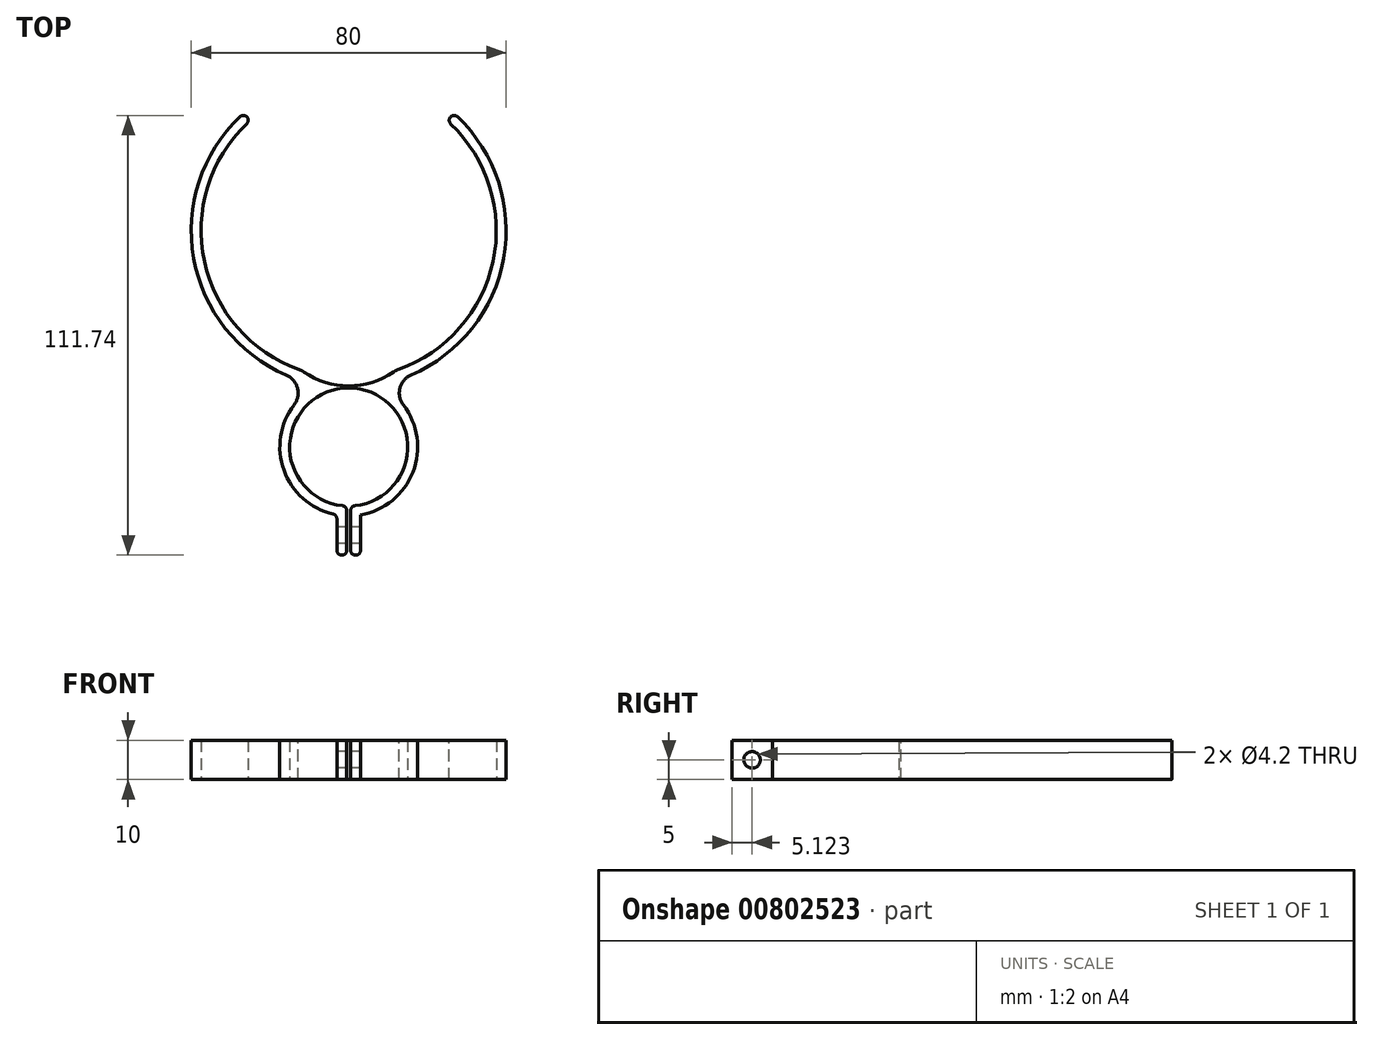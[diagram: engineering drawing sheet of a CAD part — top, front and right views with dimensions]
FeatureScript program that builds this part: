
annotation { "Feature Type Name" : "Feature", "Feature Type Description" : "" }
export const myFeature = defineFeature(function(context is Context, id is Id, definition is map)
    precondition{}
    {
        {
            var Q0;
            Q0=qCreatedBy(makeId("Top.planeOp"),FACE);
            var sketch = newSketch(context, id + "F0", { "sketchPlane" : qUnion([Q0])});
            skCircle(sketch, "E0", {"center": v(0, 0) * mm, "radius": 1.25 * mm});
            skArc(sketch, "E1", {"start": v(0, -1.25) * mm, "mid": v(-15, -16) * mm, "end": v(-0.5, -31.24) * mm});
            skArc(sketch, "E2.0", {"start": v(0, 1.25) * mm, "mid": v(-17.5, -16) * mm, "end": v(-0.5, -33.74) * mm});
            skArc(sketch, "E3", {"start": v(0, 76.25) * mm, "mid": v(-37.5, 38.75) * mm, "end": v(0, 1.25) * mm});
            skArc(sketch, "E4.0", {"start": v(0, 78.75) * mm, "mid": v(-40, 38.75) * mm, "end": v(0, -1.25) * mm});
            skLineSegment(sketch, "E5", {"start": v(0, 78.75) * mm, "end": v(0, 76.25) * mm});
            skLineSegment(sketch, "E6.bottom", {"start": v(-0.5, -31.24) * mm, "end": v(-3, -31.24) * mm});
            skLineSegment(sketch, "E6.top", {"start": v(-0.5, -43.74) * mm, "end": v(-3, -43.74) * mm});
            skLineSegment(sketch, "E6.left", {"start": v(-0.5, -31.24) * mm, "end": v(-0.5, -43.74) * mm});
            skLineSegment(sketch, "E6.right", {"start": v(-3, -31.24) * mm, "end": v(-3, -43.74) * mm});
            skPoint(sketch, "E7", {"position": v(-0.5, -33.74) * mm});
            skPoint(sketch, "E8.orphan", {"position": v(0, -31.25) * mm});
            skArc(sketch, "E9.MirrorCS", {"start": v(0, 76.25) * mm, "mid": v(37.5, 38.75) * mm, "end": v(0, 1.25) * mm});
            skArc(sketch, "E10.MirrorCS", {"start": v(0, 78.75) * mm, "mid": v(40, 38.75) * mm, "end": v(0, -1.25) * mm});
            skArc(sketch, "E11.MirrorCS", {"start": v(0, -1.25) * mm, "mid": v(15, -16) * mm, "end": v(0.5, -31.24) * mm});
            skArc(sketch, "E12.MirrorCS", {"start": v(0, 1.25) * mm, "mid": v(17.5, -16) * mm, "end": v(0.5, -33.74) * mm});
            skLineSegment(sketch, "E13.MirrorCS", {"start": v(3, -31.24) * mm, "end": v(3, -43.74) * mm});
            skLineSegment(sketch, "E14.MirrorCS", {"start": v(0.5, -31.24) * mm, "end": v(0.5, -43.74) * mm});
            skLineSegment(sketch, "E15.MirrorCS", {"start": v(0.5, -43.74) * mm, "end": v(3, -43.74) * mm});
            skSolve(sketch);
        }
        {
            var Q0;
            Q0=qSketchRegion(id+"F0",true);
            extrude(context, id + "F1", {"entities" : qUnion([Q0]), "depth" : 10 * mm, "offsetDistance" : 25 * mm});
        }
        {
            var Q0;
            Q0=qCreatedBy(makeId("Top.planeOp"),FACE);
            var sketch = newSketch(context, id + "F2", { "sketchPlane" : qUnion([Q0])});
            skLineSegment(sketch, "E16.bottom", {"start": v(-22.5, 68.75) * mm, "end": v(22.5, 68.75) * mm, "construction": true});
            skLineSegment(sketch, "E16.top", {"start": v(-22.5, 8.75) * mm, "end": v(22.5, 8.75) * mm, "construction": true});
            skLineSegment(sketch, "E16.left", {"start": v(-22.5, 68.75) * mm, "end": v(-22.5, 8.75) * mm, "construction": true});
            skLineSegment(sketch, "E16.right", {"start": v(22.5, 68.75) * mm, "end": v(22.5, 8.75) * mm, "construction": true});
            skPoint(sketch, "E17", {"position": v(0, 68.75) * mm});
            skLineSegment(sketch, "E18.bottom", {"start": v(-22.5, 68.75) * mm, "end": v(22.5, 68.75) * mm});
            skLineSegment(sketch, "E18.top", {"start": v(-22.5, 78.75) * mm, "end": v(22.5, 78.75) * mm});
            skLineSegment(sketch, "E18.left", {"start": v(-22.5, 68.75) * mm, "end": v(-22.5, 78.75) * mm});
            skLineSegment(sketch, "E18.right", {"start": v(22.5, 68.75) * mm, "end": v(22.5, 78.75) * mm});
            skSolve(sketch);
        }
        {
            var Q0;
            Q0=makeQuery(id+"F2.imprint","IMPRINT",FACE,{"disambiguationData":[TD([[makeQuery(id+"F2.imprint","IMPRINT",EDGE,{"derivedFrom":sQuery(id+"F2.wireOp",EDGE,"E18.bottom")}),1.0]])]});
            var Q1;
            Q1=makeQuery(id+"F1.opExtrude","CAP_FACE",FACE,{"disambiguationData":[OSD([sQuery(id+"F0.wireOp",EDGE,"E0"),sQuery(id+"F0.wireOp",EDGE,"E1"),sQuery(id+"F0.wireOp",EDGE,"E2.0"),sQuery(id+"F0.wireOp",EDGE,"E3"),sQuery(id+"F0.wireOp",EDGE,"E4.0"),sQuery(id+"F0.wireOp",EDGE,"E5"),sQuery(id+"F0.wireOp",EDGE,"E6.top"),sQuery(id+"F0.wireOp",EDGE,"E6.left"),sQuery(id+"F0.wireOp",EDGE,"E6.right")])],"isStart":false});
            extrude(context, id + "F3", {"entities" : qUnion([Q0]), "operationType" : NewBodyOperationType.REMOVE, "endBound" : BoundingType.UP_TO_SURFACE, "depth" : 25 * mm, "endBoundEntityFace" : qUnion([Q1]), "offsetDistance" : 25 * mm});
        }
        {
            var Q0;
            Q0=makeQuery(id+"F1.opExtrude","SWEPT_FACE",FACE,{"disambiguationData":[OSD([sQuery(id+"F0.wireOp",EDGE,"E6.right")])]});
            var sketch = newSketch(context, id + "F4", { "sketchPlane" : qUnion([Q0])});
            skCircle(sketch, "E19", {"center": v(38.62, 5) * mm, "radius": 2.1 * mm});
            skSolve(sketch);
        }
        {
            var Q0;
            Q0=makeQuery(id+"F4.imprint","IMPRINT",FACE,{"disambiguationData":[TD([[makeQuery(id+"F4.imprint","IMPRINT",EDGE,{"derivedFrom":sQuery(id+"F4.wireOp",EDGE,"E19")}),1.0]])]});
            var Q1;
            Q1=makeQuery(id+"F1.opExtrude","SWEPT_FACE",FACE,{"disambiguationData":[OSD([sQuery(id+"F0.wireOp",EDGE,"E13.MirrorCS")])]});
            extrude(context, id + "F5", {"entities" : qUnion([Q0]), "operationType" : NewBodyOperationType.REMOVE, "endBound" : BoundingType.UP_TO_SURFACE, "oppositeDirection" : true, "depth" : 25 * mm, "endBoundEntityFace" : qUnion([Q1]), "offsetDistance" : 25 * mm});
        }
        {
            var Q0;
            Q0=makeQuery(id+"F1.opExtrude","CAP_FACE",FACE,{"disambiguationData":[OSD([sQuery(id+"F0.wireOp",EDGE,"E1"),sQuery(id+"F0.wireOp",EDGE,"E2.0"),sQuery(id+"F0.wireOp",EDGE,"E3"),sQuery(id+"F0.wireOp",EDGE,"E4.0"),sQuery(id+"F0.wireOp",EDGE,"E6.top"),sQuery(id+"F0.wireOp",EDGE,"E6.left"),sQuery(id+"F0.wireOp",EDGE,"E6.right"),sQuery(id+"F0.wireOp",EDGE,"E9.MirrorCS"),sQuery(id+"F0.wireOp",EDGE,"E10.MirrorCS"),sQuery(id+"F0.wireOp",EDGE,"E11.MirrorCS"),sQuery(id+"F0.wireOp",EDGE,"E12.MirrorCS"),sQuery(id+"F0.wireOp",EDGE,"E13.MirrorCS"),sQuery(id+"F0.wireOp",EDGE,"E14.MirrorCS"),sQuery(id+"F0.wireOp",EDGE,"E15.MirrorCS")])],"isStart":false});
            var sketch = newSketch(context, id + "F6", { "sketchPlane" : qUnion([Q0])});
            skCircle(sketch, "E20", {"center": v(0, 19.25) * mm, "radius": 20 * mm});
            skPoint(sketch, "E20.centerSnap0", {"position": v(0, 1.25) * mm});
            skSolve(sketch);
        }
        {
            var Q0;
            {var subQ0=sQuery(id+"F6.wireOp",EDGE,"E20");var subQ1=makeQuery(id+"F1.opExtrude","CAP_EDGE",EDGE,{"disambiguationData":[OSD([sQuery(id+"F0.wireOp",EDGE,"E3"),sQuery(id+"F0.wireOp",EDGE,"E9.MirrorCS")])],"isStart":false});var subQ2=makeQuery(id+"F6.imprint","INTERSECT",VERTEX,{"disambiguationData":[OD(0.0)],"derivedFrom":[subQ1,subQ0]});Q0=makeQuery(id+"F6.imprint","IMPRINT",FACE,{"disambiguationData":[TD([[makeQuery(id+"F6.imprint","IMPRINT",EDGE,{"disambiguationData":[TD([[subQ2,1.0]])],"derivedFrom":subQ0}),1.0]])]});}
            var Q1;
            {var subQ0=sQuery(id+"F6.wireOp",EDGE,"PmDsQkjM-YG3i-VYAn-daZV-rx1kHTFrwvRi");var subQ1=makeQuery(id+"F1.opExtrude","CAP_EDGE",EDGE,{"disambiguationData":[OSD([sQuery(id+"F0.wireOp",EDGE,"E1"),sQuery(id+"F0.wireOp",EDGE,"E11.MirrorCS")])],"isStart":false});var subQ2=makeQuery(id+"F6.imprint","INTERSECT",VERTEX,{"disambiguationData":[OD(0.0)],"derivedFrom":[subQ1,subQ0]});Q1=makeQuery(id+"F6.imprint","IMPRINT",FACE,{"disambiguationData":[TD([[makeQuery(id+"F6.imprint","IMPRINT",EDGE,{"disambiguationData":[TD([[subQ2,-1.0]])],"derivedFrom":subQ0}),1.0]])]});}
            var Q2;
            {var subQ0=sQuery(id+"F6.wireOp",EDGE,"E20");var subQ1=makeQuery(id+"F1.opExtrude","CAP_EDGE",EDGE,{"disambiguationData":[OSD([sQuery(id+"F0.wireOp",EDGE,"E3"),sQuery(id+"F0.wireOp",EDGE,"E9.MirrorCS")])],"isStart":false});var subQ2=makeQuery(id+"F6.imprint","INTERSECT",VERTEX,{"disambiguationData":[OD(0.0)],"derivedFrom":[subQ1,subQ0]});Q2=makeQuery(id+"F6.imprint","IMPRINT",FACE,{"disambiguationData":[TD([[makeQuery(id+"F6.imprint","IMPRINT",EDGE,{"disambiguationData":[TD([[subQ2,-1.0]])],"derivedFrom":subQ0}),1.0]])]});}
            var Q3;
            {var subQ0=sQuery(id+"F6.wireOp",EDGE,"PmDsQkjM-YG3i-VYAn-daZV-rx1kHTFrwvRi");var subQ1=makeQuery(id+"F1.opExtrude","CAP_EDGE",EDGE,{"disambiguationData":[OSD([sQuery(id+"F0.wireOp",EDGE,"E1"),sQuery(id+"F0.wireOp",EDGE,"E11.MirrorCS")])],"isStart":false});var subQ2=makeQuery(id+"F6.imprint","INTERSECT",VERTEX,{"disambiguationData":[OD(0.0)],"derivedFrom":[subQ1,subQ0]});Q3=makeQuery(id+"F6.imprint","IMPRINT",FACE,{"disambiguationData":[TD([[makeQuery(id+"F6.imprint","IMPRINT",EDGE,{"disambiguationData":[TD([[subQ2,1.0]])],"derivedFrom":subQ0}),1.0]])]});}
            extrude(context, id + "F7", {"entities" : qUnion([Q0, Q1, Q2, Q3]), "operationType" : NewBodyOperationType.REMOVE, "oppositeDirection" : true, "depth" : 25 * mm, "offsetDistance" : 25 * mm});
        }
        {
            var Q0;
            Q0=makeQuery(id+"F3.boolean.opBoolean","INTERSECT",EDGE,{"derivedFrom":[makeQuery(id+"F1.opExtrude","SWEPT_FACE",FACE,{"disambiguationData":[OSD([sQuery(id+"F0.wireOp",EDGE,"E4.0")])]}),makeQuery(id+"F3.opExtrude","SWEPT_FACE",FACE,{"disambiguationData":[OSD([sQuery(id+"F2.wireOp",EDGE,"E18.left")])]})]});
            var Q1;
            Q1=makeQuery(id+"F1.opExtrude","SWEPT_EDGE",EDGE,{"disambiguationData":[OSD([sQuery(id+"F0.wireOp",EDGE,"E2.0"),sQuery(id+"F0.wireOp",EDGE,"E4.0")])]});
            var Q2;
            Q2=makeQuery(id+"F3.boolean.opBoolean","INTERSECT",EDGE,{"derivedFrom":[makeQuery(id+"F1.opExtrude","SWEPT_FACE",FACE,{"disambiguationData":[OSD([sQuery(id+"F0.wireOp",EDGE,"E4.0"),sQuery(id+"F0.wireOp",EDGE,"E10.MirrorCS")])]}),makeQuery(id+"F3.opExtrude","SWEPT_FACE",FACE,{"disambiguationData":[OSD([sQuery(id+"F2.wireOp",EDGE,"E18.right")])]})]});
            var Q3;
            Q3=makeQuery(id+"F1.opExtrude","SWEPT_EDGE",EDGE,{"disambiguationData":[OSD([sQuery(id+"F0.wireOp",EDGE,"E10.MirrorCS"),sQuery(id+"F0.wireOp",EDGE,"E12.MirrorCS")])]});
            var Q4;
            Q4=makeQuery(id+"F7.boolean.opBoolean","INTERSECT",EDGE,{"disambiguationData":[OD(0.0)],"derivedFrom":[makeQuery(id+"F1.opExtrude","SWEPT_FACE",FACE,{"disambiguationData":[OSD([sQuery(id+"F0.wireOp",EDGE,"E3"),sQuery(id+"F0.wireOp",EDGE,"E9.MirrorCS")])]}),makeQuery(id+"F7.opExtrude","SWEPT_FACE",FACE,{"disambiguationData":[OSD([sQuery(id+"F6.wireOp",EDGE,"E20")])]})]});
            var Q5;
            Q5=makeQuery(id+"F7.boolean.opBoolean","INTERSECT",EDGE,{"disambiguationData":[OD(1.0)],"derivedFrom":[makeQuery(id+"F1.opExtrude","SWEPT_FACE",FACE,{"disambiguationData":[OSD([sQuery(id+"F0.wireOp",EDGE,"E3"),sQuery(id+"F0.wireOp",EDGE,"E9.MirrorCS")])]}),makeQuery(id+"F7.opExtrude","SWEPT_FACE",FACE,{"disambiguationData":[OSD([sQuery(id+"F6.wireOp",EDGE,"E20")])]})]});
            var Q6;
            Q6=makeQuery(id+"F7.boolean.opBoolean","INTERSECT",EDGE,{"disambiguationData":[OD(0.0)],"derivedFrom":[makeQuery(id+"F1.opExtrude","SWEPT_FACE",FACE,{"disambiguationData":[OSD([sQuery(id+"F0.wireOp",EDGE,"E1"),sQuery(id+"F0.wireOp",EDGE,"E11.MirrorCS")])]}),makeQuery(id+"F7.opExtrude","SWEPT_FACE",FACE,{"disambiguationData":[OSD([sQuery(id+"F6.wireOp",EDGE,"PmDsQkjM-YG3i-VYAn-daZV-rx1kHTFrwvRi")])]})]});
            var Q7;
            Q7=makeQuery(id+"F7.boolean.opBoolean","INTERSECT",EDGE,{"disambiguationData":[OD(1.0)],"derivedFrom":[makeQuery(id+"F1.opExtrude","SWEPT_FACE",FACE,{"disambiguationData":[OSD([sQuery(id+"F0.wireOp",EDGE,"E1"),sQuery(id+"F0.wireOp",EDGE,"E11.MirrorCS")])]}),makeQuery(id+"F7.opExtrude","SWEPT_FACE",FACE,{"disambiguationData":[OSD([sQuery(id+"F6.wireOp",EDGE,"PmDsQkjM-YG3i-VYAn-daZV-rx1kHTFrwvRi")])]})]});
            fillet(context, id + "F8", {"entities" : qUnion([Q0, Q1, Q2, Q3, Q4, Q5, Q6, Q7]), "radius" : 5 * mm, "tangentPropagation" : true, "allowEdgeOverflow" : false});
        }
        {
            var Q0;
            Q0=makeQuery(id+"F1.opExtrude","SWEPT_EDGE",EDGE,{"disambiguationData":[OSD([sQuery(id+"F0.wireOp",EDGE,"E2.0"),sQuery(id+"F0.wireOp",EDGE,"E6.right")])]});
            var Q1;
            Q1=makeQuery(id+"F1.opExtrude","SWEPT_EDGE",EDGE,{"disambiguationData":[OSD([sQuery(id+"F0.wireOp",EDGE,"E1"),sQuery(id+"F0.wireOp",EDGE,"E6.bottom"),sQuery(id+"F0.wireOp",EDGE,"E6.left")])]});
            var Q2;
            Q2=makeQuery(id+"F1.opExtrude","SWEPT_EDGE",EDGE,{"disambiguationData":[OSD([sQuery(id+"F0.wireOp",EDGE,"E6.top"),sQuery(id+"F0.wireOp",EDGE,"E6.left")])]});
            var Q3;
            Q3=makeQuery(id+"F1.opExtrude","SWEPT_EDGE",EDGE,{"disambiguationData":[OSD([sQuery(id+"F0.wireOp",EDGE,"E6.top"),sQuery(id+"F0.wireOp",EDGE,"E6.right")])]});
            var Q4;
            Q4=makeQuery(id+"F8.opFillet","BLEND_EDGE",EDGE,{"blendedFrom":[makeQuery(id+"F3.boolean.opBoolean","INTERSECT",EDGE,{"derivedFrom":[makeQuery(id+"F1.opExtrude","SWEPT_FACE",FACE,{"disambiguationData":[OSD([sQuery(id+"F0.wireOp",EDGE,"E4.0")])]}),makeQuery(id+"F3.opExtrude","SWEPT_FACE",FACE,{"disambiguationData":[OSD([sQuery(id+"F2.wireOp",EDGE,"E18.left")])]})]}),makeQuery(id+"F1.opExtrude","SWEPT_FACE",FACE,{"disambiguationData":[OSD([sQuery(id+"F0.wireOp",EDGE,"E3")])]})],"blendedInto":[makeQuery(id+"F1.opExtrude","SWEPT_FACE",FACE,{"disambiguationData":[OSD([sQuery(id+"F0.wireOp",EDGE,"E3")])]})]});
            var Q5;
            Q5=makeQuery(id+"F1.opExtrude","SWEPT_EDGE",EDGE,{"disambiguationData":[OSD([sQuery(id+"F0.wireOp",EDGE,"E11.MirrorCS"),sQuery(id+"F0.wireOp",EDGE,"E14.MirrorCS")])]});
            var Q6;
            Q6=makeQuery(id+"F1.opExtrude","SWEPT_EDGE",EDGE,{"disambiguationData":[OSD([sQuery(id+"F0.wireOp",EDGE,"E14.MirrorCS"),sQuery(id+"F0.wireOp",EDGE,"E15.MirrorCS")])]});
            var Q7;
            Q7=makeQuery(id+"F1.opExtrude","SWEPT_EDGE",EDGE,{"disambiguationData":[OSD([sQuery(id+"F0.wireOp",EDGE,"E13.MirrorCS"),sQuery(id+"F0.wireOp",EDGE,"E15.MirrorCS")])]});
            var Q8;
            {var subQ5=sQuery(id+"F0.wireOp",EDGE,"E10.MirrorCS");var subQ6=sQuery(id+"F0.wireOp",EDGE,"E9.MirrorCS");var subQ10=sQuery(id+"F0.wireOp",EDGE,"E4.0");var subQ11=sQuery(id+"F0.wireOp",EDGE,"E3");var subQ14=makeQuery(id+"F3.opExtrude","SWEPT_FACE",FACE,{"disambiguationData":[OSD([sQuery(id+"F2.wireOp",EDGE,"E18.right")])]});Q8=makeQuery(id+"F8.opFillet","BLEND_EDGE",EDGE,{"blendedFrom":[makeQuery(id+"F3.boolean.opBoolean","INTERSECT",EDGE,{"derivedFrom":[makeQuery(id+"F1.opExtrude","SWEPT_FACE",FACE,{"disambiguationData":[OSD([subQ10,subQ5])]}),subQ14]}),makeQuery(id+"F7.boolean.opBoolean","SPLIT",FACE,{"disambiguationData":[TD([makeQuery(id+"F3.boolean.opBoolean","COPY",FACE,{"derivedFrom":subQ14})])],"derivedFrom":makeQuery(id+"F1.opExtrude","SWEPT_FACE",FACE,{"disambiguationData":[OSD([subQ11,subQ6])]})})],"blendedInto":[makeQuery(id+"F7.boolean.opBoolean","SPLIT",FACE,{"disambiguationData":[TD([makeQuery(id+"F3.boolean.opBoolean","COPY",FACE,{"derivedFrom":subQ14})])],"derivedFrom":makeQuery(id+"F1.opExtrude","SWEPT_FACE",FACE,{"disambiguationData":[OSD([subQ11,subQ6])]})})]});}
            fillet(context, id + "F9", {"entities" : qUnion([Q0, Q1, Q2, Q3, Q4, Q5, Q6, Q7, Q8]), "radius" : 1.25 * mm, "tangentPropagation" : true, "allowEdgeOverflow" : false});
        }
    });
